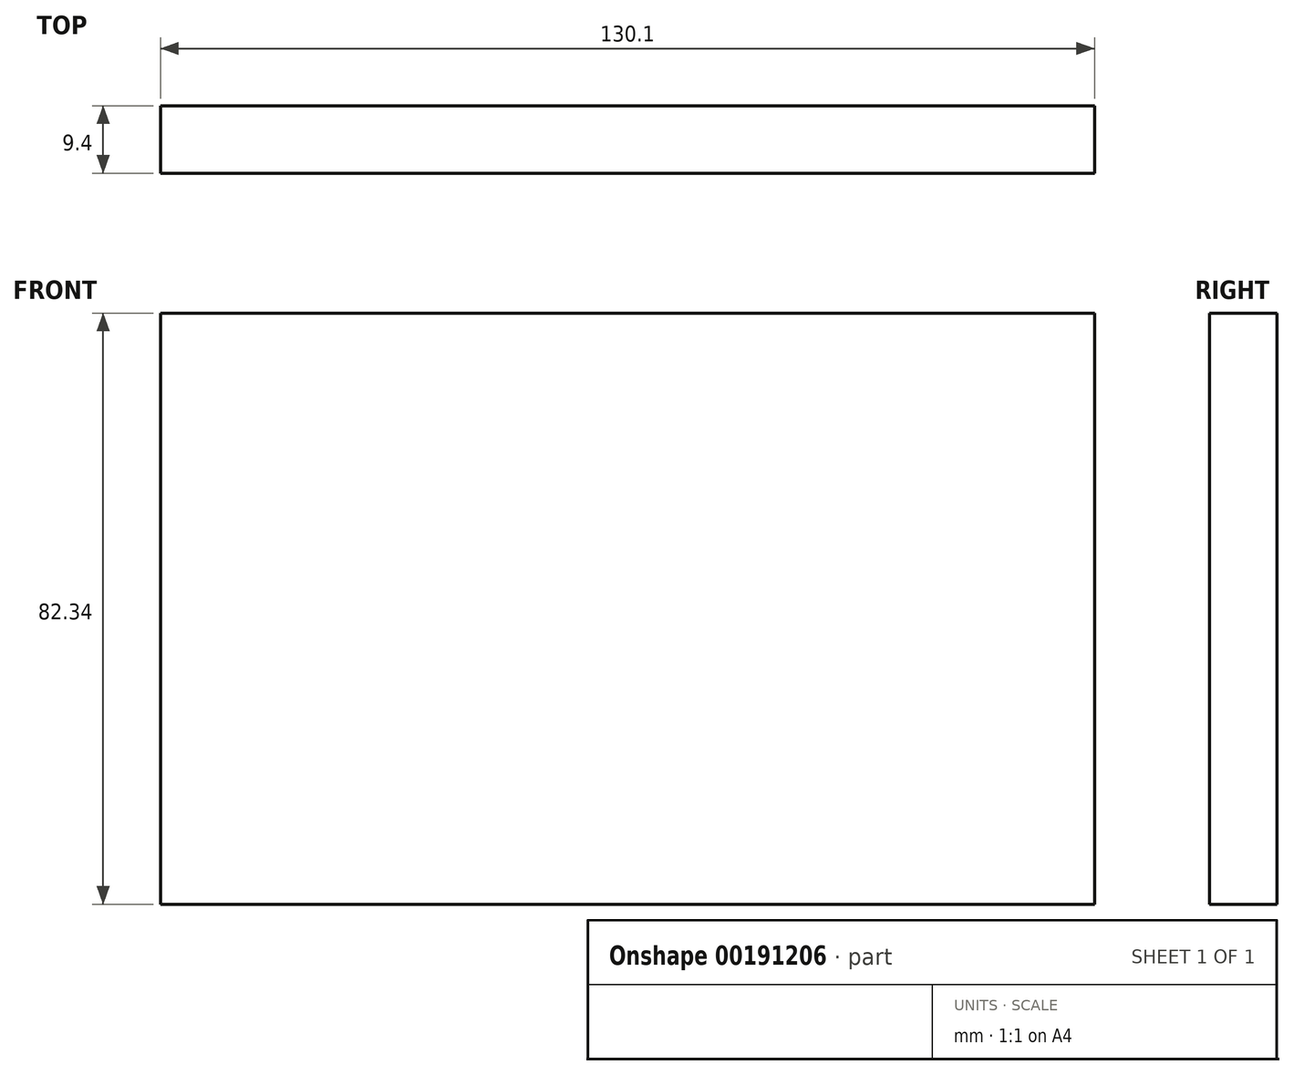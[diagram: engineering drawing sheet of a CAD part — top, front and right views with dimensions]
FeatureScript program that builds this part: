
annotation { "Feature Type Name" : "Feature", "Feature Type Description" : "" }
export const myFeature = defineFeature(function(context is Context, id is Id, definition is map)
    precondition{}
    {
        {
            var Q0;
            Q0=qCreatedBy(makeId("Front.planeOp"),FACE);
            var sketch = newSketch(context, id + "F0", { "sketchPlane" : qUnion([Q0])});
            skLineSegment(sketch, "E0.bottom", {"start": v(-65.81, 61.36) * mm, "end": v(64.29, 61.36) * mm});
            skLineSegment(sketch, "E0.top", {"start": v(-65.81, -20.98) * mm, "end": v(64.29, -20.98) * mm});
            skLineSegment(sketch, "E0.left", {"start": v(-65.81, 61.36) * mm, "end": v(-65.81, -20.98) * mm});
            skLineSegment(sketch, "E0.right", {"start": v(64.29, 61.36) * mm, "end": v(64.29, -20.98) * mm});
            skSolve(sketch);
        }
        {
            var Q0;
            Q0=makeQuery(id+"F0.imprint","IMPRINT",FACE,{"disambiguationData":[TD([[makeQuery(id+"F0.imprint","IMPRINT",EDGE,{"derivedFrom":sQuery(id+"F0.wireOp",EDGE,"E0.bottom")}),-1.0]])]});
            extrude(context, id + "F1", {"entities" : qUnion([Q0]), "depth" : 9.4 * mm});
        }
    });
